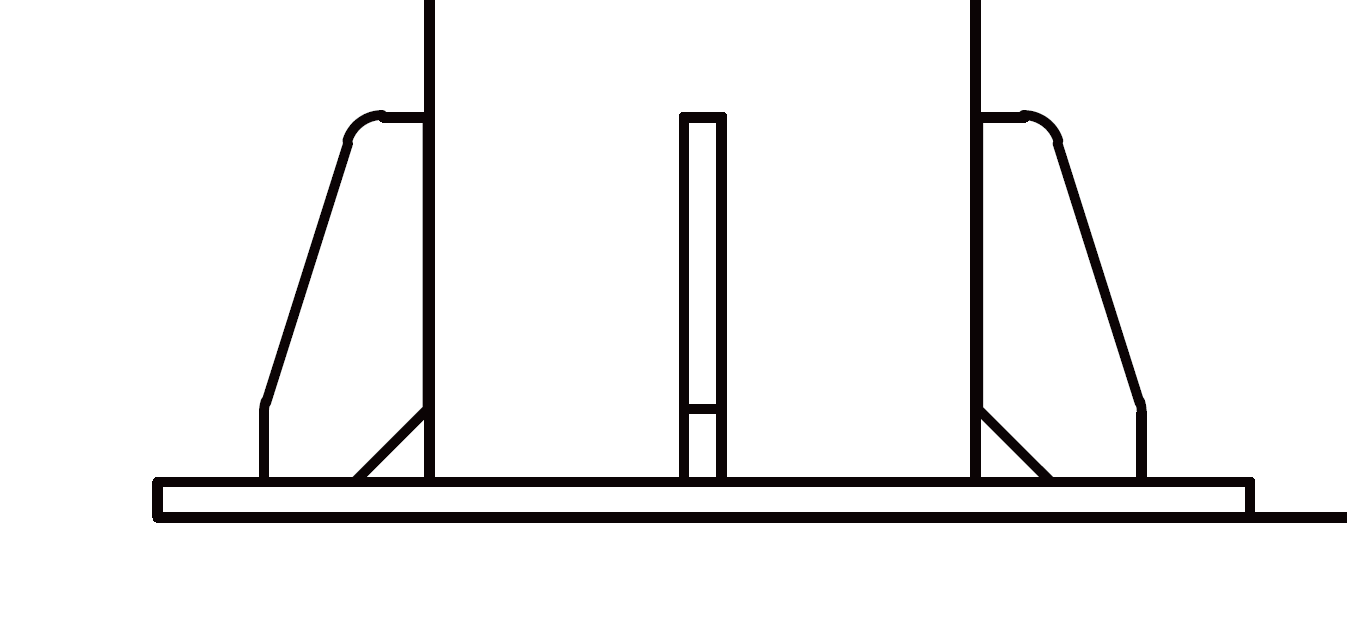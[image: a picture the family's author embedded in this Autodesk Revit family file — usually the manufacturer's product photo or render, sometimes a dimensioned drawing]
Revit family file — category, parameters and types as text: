
# Revit family: Lin2-16.4ft
name_source: partatom
category: Lighting Fixtures
units: mm (PartAtom-declared; Revit-internal decimal feet)

## family parameters
Always vertical = Yes
Cut with Voids When Loaded = No
Light Source = Yes
Maintain Annotation Orientation = No
OmniClass Number = 23.80.70.00
OmniClass Title = Lighting
Part Type = Normal
Room Calculation Point = No
Round Connector Dimension = Use Diameter
Shared = No
Work Plane-Based = No

## types (16) — shared parameters
CRI = 80
Color Filter = 16777215
Default Elevation = 0' - 0"
Dimming Lamp Color Temperature Shift = <None>
H = 16' - 4 13/16"
IP Rating = IP65
Input Voltage = 120-277V
Lamp = LED
Load Classification = Lighting
Manufacturer = Above All Lighting
Power Factor = 0.9
Tilt Angle = 90.00°
URL = https://www.abovealllighting.com

## per-type parameters (varying)
| type | Model | Photometric Web File | Wattage Comments |
| LIN2-70W-3000K-II-16.4ft | LIN2-7030801-II-BK | LIN2-7030801-II-BK.IES | 70W |
| LIN2-70W-3000K-III-16.4ft | LIN2-7030801-III-BK | LIN2-7030801-III-BK.IES | 70W |
| LIN2-70W-3000K-IV-16.4ft | LIN2-7030801-IV-BK | LIN2-7030801-IV-BK.IES | 70W |
| LIN2-70W-3000K-V-16.4ft | LIN2-7030801-V-BK | LIN2-7030801-V-BK.IES | 70W |
| LIN2-80W-3000K-II-16.4ft | LIN2-8030801-II-BK | LIN2-8030801-II-BK.IES | 80W |
| LIN2-80W-3000K-III-16.4ft | LIN2-8030801-III-BK | LIN2-8030801-III-BK.IES | 80W |
| LIN2-80W-3000K-IV-16.4ft | LIN2-8030801-IV-BK | LIN2-8030801-IV-BK.IES | 80W |
| LIN2-80W-3000K-V-16.4ft | LIN2-8030801-V-BK | LIN2-8030801-V-BK.IES | 80W |
| LIN2-100W-3000K-II-16.4ft | LIN2-10030801-II-BK | LIN2-10030801-II-BK.IES | 100W |
| LIN2-100W-3000K-III-16.4ft | LIN2-10030801-III-BK | LIN2-10030801-III-BK.IES | 100W |
| LIN2-100W-3000K-IV-16.4ft | LIN2-10030801-IV-BK | LIN2-10030801-IV-BK.IES | 100W |
| LIN2-100W-3000K-V-16.4ft | LIN2-10030801-V-BK | LIN2-10030801-V-BK.IES | 100W |
| LIN2-120W-3000K-II-16.4ft | LIN2-12030801-II-BK | LIN2-12030801-II-BK.IES | 120W |
| LIN2-120W-3000K-III-16.4ft | LIN2-12030801-III-BK | LIN2-12030801-III-BK.IES | 120W |
| LIN2-120W-3000K-IV-16.4ft | LIN2-12030801-IV-BK | LIN2-12030801-IV-BK.IES | 120W |
| LIN2-120W-3000K-V-16.4ft | LIN2-12030801-V-BK | LIN2-12030801-V-BK.IES | 120W |

## geometry (parser evidence)
native form markers: Sweep x2
no freeform markers — native parametric forms only
